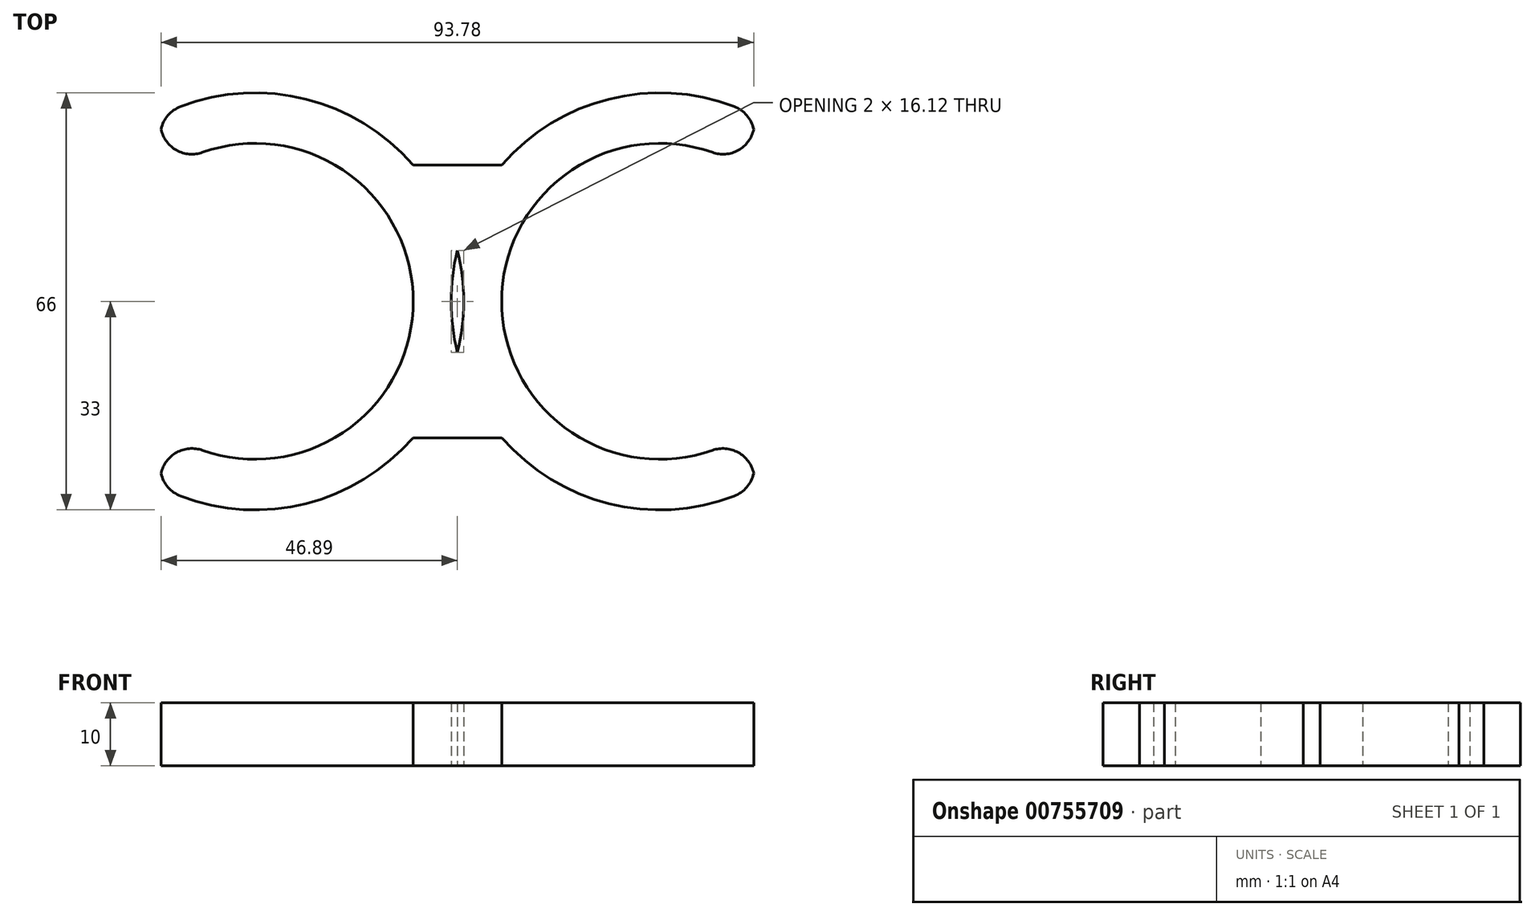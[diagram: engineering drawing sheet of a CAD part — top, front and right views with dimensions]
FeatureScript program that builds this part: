
annotation { "Feature Type Name" : "Feature", "Feature Type Description" : "" }
export const myFeature = defineFeature(function(context is Context, id is Id, definition is map)
    precondition{}
    {
        {
            var Q0;
            Q0=qCreatedBy(makeId("Top.planeOp"),FACE);
            var sketch = newSketch(context, id + "F0", { "sketchPlane" : qUnion([Q0])});
            skArc(sketch, "E0", {"start": v(-47, -20) * mm, "mid": v(-7, 0) * mm, "end": v(-47, 20) * mm});
            skArc(sketch, "E1", {"start": v(-47, -29.4) * mm, "mid": v(1, 0) * mm, "end": v(-47, 29.4) * mm});
            skLineSegment(sketch, "E2", {"start": v(-47, 29.4) * mm, "end": v(-47, 20) * mm});
            skLineSegment(sketch, "E3.trimOffspring", {"start": v(-47, -20) * mm, "end": v(-47, -29.4) * mm});
            skArc(sketch, "E4.MirrorCS", {"start": v(47, -20) * mm, "mid": v(7, 0) * mm, "end": v(47, 20) * mm});
            skArc(sketch, "E5.MirrorCS", {"start": v(47, -29.4) * mm, "mid": v(-1, 0) * mm, "end": v(47, 29.4) * mm});
            skLineSegment(sketch, "E6.MirrorCS", {"start": v(47, 29.4) * mm, "end": v(47, 20) * mm});
            skLineSegment(sketch, "E7.MirrorCS", {"start": v(47, -20) * mm, "end": v(47, -29.4) * mm});
            skLineSegment(sketch, "E8.bottom", {"start": v(-7.04, 21.58) * mm, "end": v(7.04, 21.58) * mm});
            skLineSegment(sketch, "E8.top", {"start": v(-7.04, -21.58) * mm, "end": v(7.04, -21.58) * mm});
            skLineSegment(sketch, "E8.left", {"start": v(-7.04, 21.58) * mm, "end": v(-7.04, -21.58) * mm});
            skLineSegment(sketch, "E8.right", {"start": v(7.04, 21.58) * mm, "end": v(7.04, -21.58) * mm});
            skPoint(sketch, "E8.middle", {"position": v(0, 0) * mm});
            skSolve(sketch);
        }
        {
            var Q0;
            Q0=qSketchRegion(id+"F0",true);
            var Q1;
            {var subQ0=sQuery(id+"F0.wireOp",EDGE,"E5.MirrorCS");var subQ1=sQuery(id+"F0.wireOp",EDGE,"E1");var subQ2=makeQuery(id+"F0.imprint","INTERSECT",VERTEX,{"disambiguationData":[OD(0.0)],"derivedFrom":[subQ1,subQ0]});Q1=makeQuery(id+"F0.imprint","IMPRINT",FACE,{"disambiguationData":[TD([[makeQuery(id+"F0.imprint","IMPRINT",EDGE,{"disambiguationData":[TD([[subQ2,-1.0]])],"derivedFrom":subQ1}),1.0]])]});}
            extrude(context, id + "F1", {"entities" : qUnion([Q0, Q1]), "depth" : 5 * mm, "offsetDistance" : 25 * mm, "hasSecondDirection" : true, "secondDirectionOppositeDirection" : true, "secondDirectionDepth" : 5 * mm});
        }
        {
            var Q0;
            Q0=makeQuery(id+"F1.opExtrude","SWEPT_EDGE",EDGE,{"disambiguationData":[OSD([sQuery(id+"F0.wireOp",EDGE,"E0"),sQuery(id+"F0.wireOp",EDGE,"E2")])]});
            var Q1;
            Q1=makeQuery(id+"F1.opExtrude","SWEPT_EDGE",EDGE,{"disambiguationData":[OSD([sQuery(id+"F0.wireOp",EDGE,"E1"),sQuery(id+"F0.wireOp",EDGE,"E3.trimOffspring")])]});
            var Q2;
            Q2=makeQuery(id+"F1.opExtrude","SWEPT_EDGE",EDGE,{"disambiguationData":[OSD([sQuery(id+"F0.wireOp",EDGE,"E0"),sQuery(id+"F0.wireOp",EDGE,"E3.trimOffspring")])]});
            var Q3;
            Q3=makeQuery(id+"F1.opExtrude","SWEPT_EDGE",EDGE,{"disambiguationData":[OSD([sQuery(id+"F0.wireOp",EDGE,"E1"),sQuery(id+"F0.wireOp",EDGE,"E2")])]});
            var Q4;
            Q4=makeQuery(id+"F1.opExtrude","SWEPT_EDGE",EDGE,{"disambiguationData":[OSD([sQuery(id+"F0.wireOp",EDGE,"E5.MirrorCS"),sQuery(id+"F0.wireOp",EDGE,"E7.MirrorCS")])]});
            var Q5;
            Q5=makeQuery(id+"F1.opExtrude","SWEPT_EDGE",EDGE,{"disambiguationData":[OSD([sQuery(id+"F0.wireOp",EDGE,"E4.MirrorCS"),sQuery(id+"F0.wireOp",EDGE,"E7.MirrorCS")])]});
            var Q6;
            Q6=makeQuery(id+"F1.opExtrude","SWEPT_EDGE",EDGE,{"disambiguationData":[OSD([sQuery(id+"F0.wireOp",EDGE,"E4.MirrorCS"),sQuery(id+"F0.wireOp",EDGE,"E6.MirrorCS")])]});
            var Q7;
            Q7=makeQuery(id+"F1.opExtrude","SWEPT_EDGE",EDGE,{"disambiguationData":[OSD([sQuery(id+"F0.wireOp",EDGE,"E5.MirrorCS"),sQuery(id+"F0.wireOp",EDGE,"E6.MirrorCS")])]});
            fillet(context, id + "F2", {"entities" : qUnion([Q0, Q1, Q2, Q3, Q4, Q5, Q6, Q7]), "radius" : 5 * mm, "tangentPropagation" : true, "allowEdgeOverflow" : false});
        }
    });
